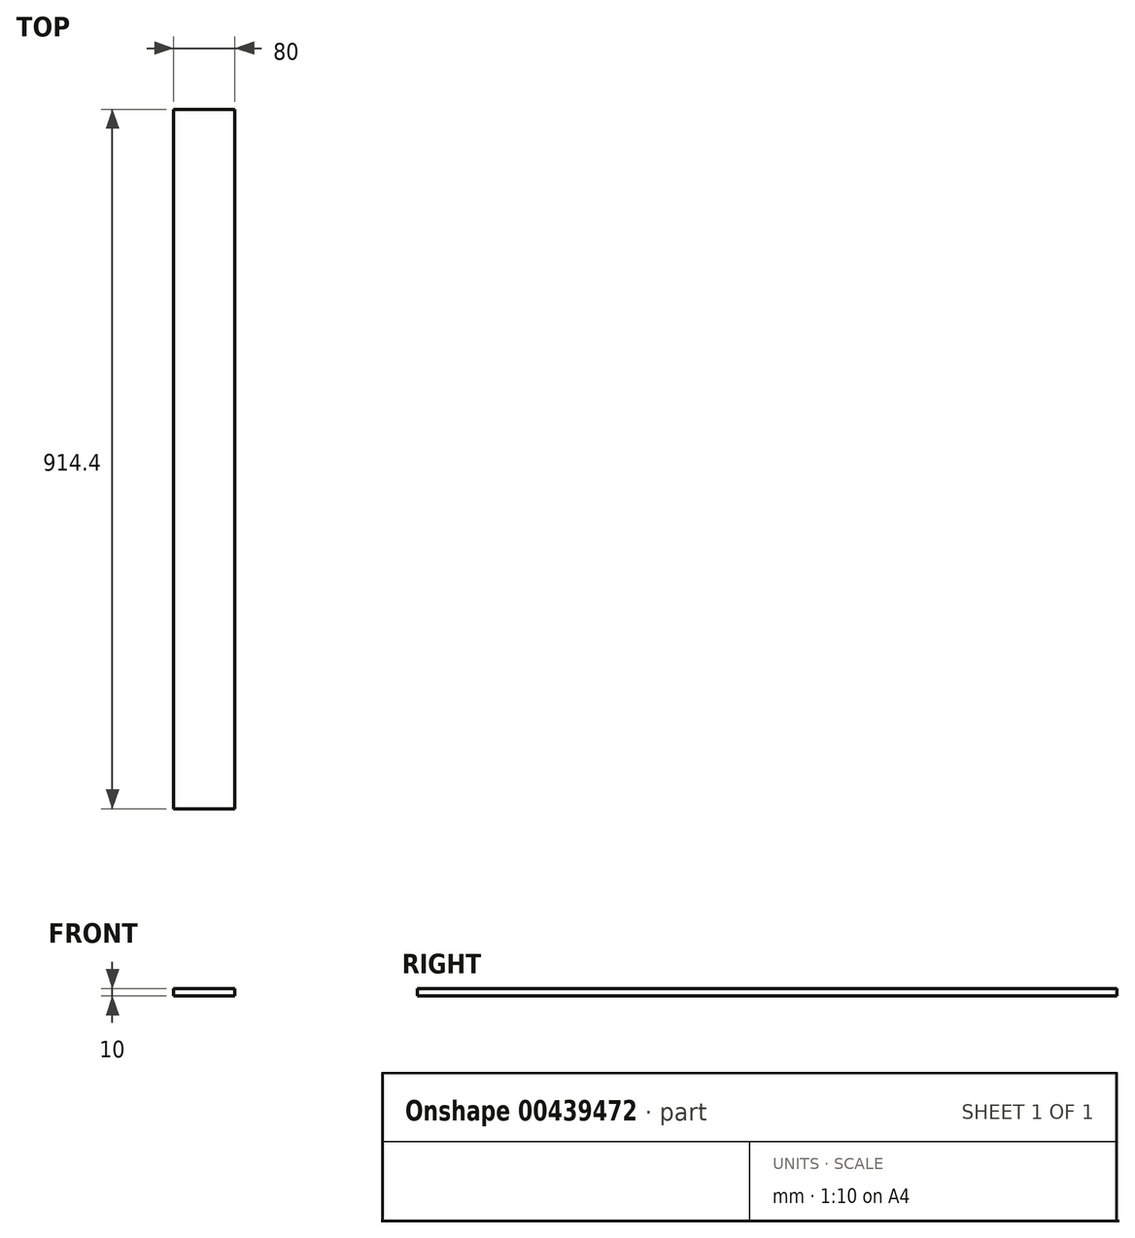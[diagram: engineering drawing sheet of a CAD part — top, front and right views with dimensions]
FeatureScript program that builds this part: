
annotation { "Feature Type Name" : "Feature", "Feature Type Description" : "" }
export const myFeature = defineFeature(function(context is Context, id is Id, definition is map)
    precondition{}
    {
        {
            var Q0;
            Q0=qCreatedBy(makeId("Front.planeOp"),FACE);
            var sketch = newSketch(context, id + "F0", { "sketchPlane" : qUnion([Q0])});
            skLineSegment(sketch, "E0.bottom", {"start": v(40, 5) * mm, "end": v(-40, 5) * mm});
            skLineSegment(sketch, "E0.top", {"start": v(40, -5) * mm, "end": v(-40, -5) * mm});
            skLineSegment(sketch, "E0.left", {"start": v(40, 5) * mm, "end": v(40, -5) * mm});
            skLineSegment(sketch, "E0.right", {"start": v(-40, 5) * mm, "end": v(-40, -5) * mm});
            skPoint(sketch, "E0.middle", {"position": v(0, 0) * mm});
            skSolve(sketch);
        }
        {
            var Q0;
            Q0 = qSketchRegion(id + "F0", true);
            extrude(context, id + "F1", {"entities" : qUnion([Q0]), "depth" : 914.4 * mm});
        }
    });
